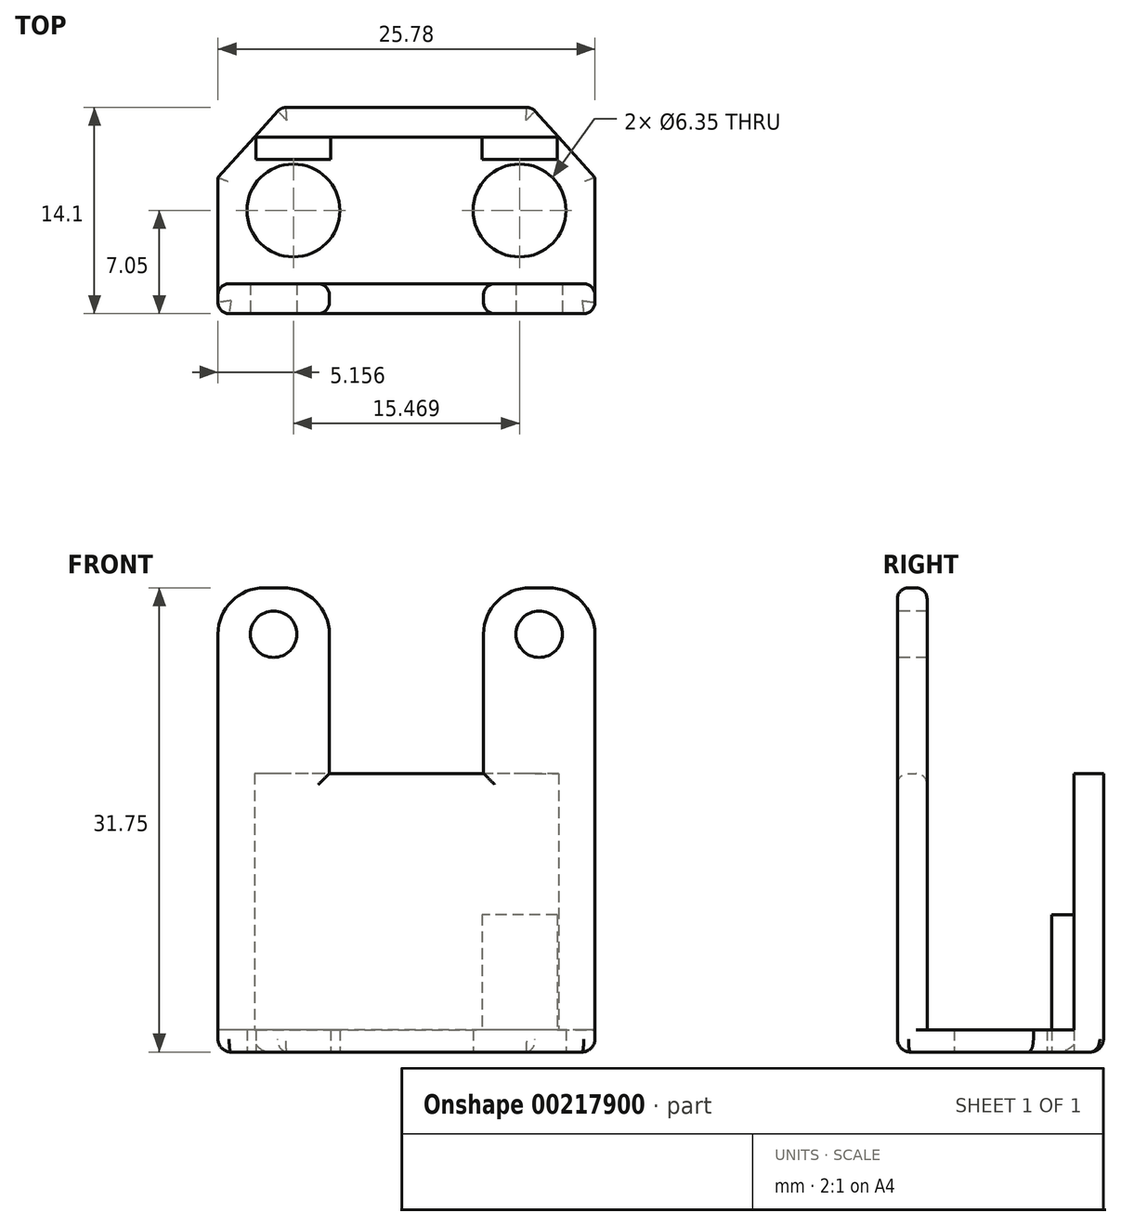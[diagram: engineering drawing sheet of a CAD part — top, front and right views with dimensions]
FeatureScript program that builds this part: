
annotation { "Feature Type Name" : "Feature", "Feature Type Description" : "" }
export const myFeature = defineFeature(function(context is Context, id is Id, definition is map)
    precondition{}
    {
        {
            var Q0;
            Q0=qCreatedBy(makeId("Top.planeOp"),FACE);
            var sketch = newSketch(context, id + "F0", { "sketchPlane" : qUnion([Q0])});
            skLineSegment(sketch, "E0.bottom", {"start": v(10.4, 5.02) * mm, "end": v(-10.4, 5.02) * mm});
            skLineSegment(sketch, "E0.top", {"start": v(12.9, -5.02) * mm, "end": v(-12.9, -5.02) * mm});
            skLineSegment(sketch, "E0.left", {"start": v(12.9, 2.26) * mm, "end": v(12.9, -7.05) * mm});
            skLineSegment(sketch, "E0.right", {"start": v(-12.9, 2.26) * mm, "end": v(-12.9, -7.05) * mm});
            skPoint(sketch, "E0.middle", {"position": v(0, 0) * mm});
            skLineSegment(sketch, "E1.0", {"start": v(14.92, 7.05) * mm, "end": v(-14.92, 7.05) * mm});
            skLineSegment(sketch, "E1.1", {"start": v(14.92, 7.05) * mm, "end": v(14.92, -7.05) * mm});
            skLineSegment(sketch, "E1.2", {"start": v(14.92, -7.05) * mm, "end": v(-14.92, -7.05) * mm});
            skLineSegment(sketch, "E1.3", {"start": v(-14.92, 7.05) * mm, "end": v(-14.92, -7.05) * mm});
            skPoint(sketch, "E2", {"position": v(-7.73, 0) * mm});
            skPoint(sketch, "E2.positionSnap0", {"position": v(-12.9, 0) * mm});
            skLineSegment(sketch, "E3", {"start": v(0, 5.02) * mm, "end": v(0, -5.02) * mm, "construction": true});
            skPoint(sketch, "E4.MirrorP", {"position": v(7.73, 0) * mm});
            skLineSegment(sketch, "E5", {"start": v(-11.78, 3.5) * mm, "end": v(11.78, 3.5) * mm});
            skLineSegment(sketch, "E6", {"start": v(-7.73, 3.5) * mm, "end": v(-7.73, 5.02) * mm, "construction": true});
            skLineSegment(sketch, "E7", {"start": v(-7.73, 3.5) * mm, "end": v(-10.3, 3.5) * mm});
            skLineSegment(sketch, "E8", {"start": v(-10.3, 3.5) * mm, "end": v(-10.3, 5.02) * mm});
            skLineSegment(sketch, "E9.MirrorCS", {"start": v(-5.17, 3.5) * mm, "end": v(-5.17, 5.02) * mm});
            skLineSegment(sketch, "E10.MirrorCS", {"start": v(5.17, 3.5) * mm, "end": v(5.17, 5.02) * mm});
            skLineSegment(sketch, "E11.MirrorCS", {"start": v(10.3, 3.5) * mm, "end": v(10.3, 5.02) * mm});
            skLineSegment(sketch, "E12.MirrorCS", {"start": v(7.73, 3.5) * mm, "end": v(10.3, 3.5) * mm});
            skLineSegment(sketch, "E13.MirrorCS", {"start": v(7.73, 3.5) * mm, "end": v(7.73, 5.02) * mm, "construction": true});
            skPoint(sketch, "E14.endSnap0", {"position": v(-9.02, 3.5) * mm});
            skLineSegment(sketch, "E15", {"start": v(-14.92, 7.05) * mm, "end": v(-8.57, 7.05) * mm});
            skLineSegment(sketch, "E16", {"start": v(-8.57, 7.05) * mm, "end": v(-14.92, 0) * mm});
            skPoint(sketch, "E17.orphan", {"position": v(-12.9, 5.02) * mm});
            skLineSegment(sketch, "E18.MirrorCS", {"start": v(8.57, 7.05) * mm, "end": v(14.92, 0) * mm});
            skPoint(sketch, "E19.orphan", {"position": v(12.9, 5.02) * mm});
            skLineSegment(sketch, "E20", {"start": v(-12.9, -5.02) * mm, "end": v(-14.92, -5.02) * mm});
            skLineSegment(sketch, "E21", {"start": v(12.9, -5.02) * mm, "end": v(14.92, -5.02) * mm});
            skLineSegment(sketch, "E22", {"start": v(-5.27, -5.02) * mm, "end": v(-5.27, -7.05) * mm});
            skLineSegment(sketch, "E23.MirrorCS", {"start": v(5.27, -5.02) * mm, "end": v(5.27, -7.05) * mm});
            skSolve(sketch);
        }
        {
            var Q0;
            Q0=makeQuery(id+"F0.imprint","IMPRINT",FACE,{"disambiguationData":[TD([[makeQuery(id+"F0.imprint","IMPRINT",EDGE,{"derivedFrom":sQuery(id+"F0.wireOp",EDGE,"E0.bottom")}),-1.0]])]});
            var Q1;
            {var subQ0=sQuery(id+"F0.wireOp",EDGE,"E0.top");Q1=makeQuery(id+"F0.imprint","IMPRINT",FACE,{"disambiguationData":[TD([[makeQuery(id+"F0.imprint","IMPRINT",EDGE,{"derivedFrom":subQ0}),-1.0]])]});}
            var Q2;
            {var subQ0=sQuery(id+"F0.wireOp",EDGE,"E0.bottom");Q2=makeQuery(id+"F0.imprint","IMPRINT",FACE,{"disambiguationData":[TD([[makeQuery(id+"F0.imprint","IMPRINT",EDGE,{"derivedFrom":subQ0}),1.0]])]});}
            var Q3;
            {var subQ1=sQuery(id+"F0.wireOp",EDGE,"E7");Q3=makeQuery(id+"F0.imprint","IMPRINT",FACE,{"disambiguationData":[TD([[makeQuery(id+"F0.imprint","IMPRINT",EDGE,{"derivedFrom":subQ1}),-1.0]])]});}
            var Q4;
            {var subQ0=sQuery(id+"F0.wireOp",EDGE,"E10.MirrorCS");Q4=makeQuery(id+"F0.imprint","IMPRINT",FACE,{"disambiguationData":[TD([[makeQuery(id+"F0.imprint","IMPRINT",EDGE,{"derivedFrom":subQ0}),-1.0]])]});}
            extrude(context, id + "F1", {"entities" : qUnion([Q0, Q1, Q2, Q3, Q4]), "depth" : 1.52 * mm});
        }
        {
            var Q0;
            Q0=makeQuery(id+"F0.imprint","IMPRINT",FACE,{"disambiguationData":[TD([[makeQuery(id+"F0.imprint","IMPRINT",EDGE,{"derivedFrom":sQuery(id+"F0.wireOp",EDGE,"E0.bottom")}),-1.0]])]});
            var Q1;
            Q1=makeQuery(id+"F0.imprint","IMPRINT",FACE,{"disambiguationData":[TD([[makeQuery(id+"F0.imprint","IMPRINT",EDGE,{"derivedFrom":sQuery(id+"F0.wireOp",EDGE,"E0.top")}),1.0]])]});
            extrude(context, id + "F2", {"entities" : qUnion([Q0, Q1]), "operationType" : NewBodyOperationType.ADD, "depth" : 19.05 * mm});
        }
        {
            var Q0;
            {var subQ0=sQuery(id+"F0.wireOp",EDGE,"E7");Q0=makeQuery(id+"F0.imprint","IMPRINT",FACE,{"disambiguationData":[TD([[makeQuery(id+"F0.imprint","IMPRINT",EDGE,{"derivedFrom":subQ0}),-1.0]])]});}
            var Q1;
            {var subQ1=sQuery(id+"F0.wireOp",EDGE,"E10.MirrorCS");Q1=makeQuery(id+"F0.imprint","IMPRINT",FACE,{"disambiguationData":[TD([[makeQuery(id+"F0.imprint","IMPRINT",EDGE,{"derivedFrom":subQ1}),-1.0]])]});}
            extrude(context, id + "F3", {"entities" : qUnion([Q0, Q1]), "operationType" : NewBodyOperationType.ADD, "depth" : 9.4 * mm});
        }
        {
            var Q0;
            Q0=sQuery(id+"F0.wireOp",VERTEX,"E2");
            var Q1;
            Q1=sQuery(id+"F0.wireOp",VERTEX,"E4.MirrorP");
            var Q2;
            Q2=makeQuery(id+"F1.opExtrude","SWEPT_BODY",BODY,{"disambiguationData":[OSD([sQuery(id+"F0.wireOp",EDGE,"E1.0"),sQuery(id+"F0.wireOp",EDGE,"E1.1"),sQuery(id+"F0.wireOp",EDGE,"E1.2"),sQuery(id+"F0.wireOp",EDGE,"E1.3")])]});
            hole(context, id + "F4", {"style" : HoleStyle.SIMPLE, "endStyle" : HoleEndStyle.BLIND, "oppositeDirection" : true, "holeDiameter" : 6.35 * mm, "holeDepth" : 6.73 * mm, "locations" : qUnion([Q0, Q1]), "scope" : qUnion([Q2])});
        }
        {
            var Q0;
            {var subQ3=sQuery(id+"F0.wireOp",EDGE,"E22");Q0=makeQuery(id+"F0.imprint","IMPRINT",FACE,{"disambiguationData":[TD([[makeQuery(id+"F0.imprint","IMPRINT",EDGE,{"derivedFrom":subQ3}),-1.0]])]});}
            var Q1;
            {var subQ3=sQuery(id+"F0.wireOp",EDGE,"E23.MirrorCS");Q1=makeQuery(id+"F0.imprint","IMPRINT",FACE,{"disambiguationData":[TD([[makeQuery(id+"F0.imprint","IMPRINT",EDGE,{"derivedFrom":subQ3}),1.0]])]});}
            extrude(context, id + "F5", {"entities" : qUnion([Q0, Q1]), "operationType" : NewBodyOperationType.ADD, "depth" : 31.75 * mm});
        }
        {
            var Q0;
            {var subQ0=sQuery(id+"F0.wireOp",EDGE,"E1.2");Q0=makeQuery(id+"F5.boolean.opBoolean","MERGE",FACE,{"derivedFrom":[makeQuery(id+"F2.opExtrude","SWEPT_FACE",FACE,{"disambiguationData":[OSD([subQ0])]}),makeQuery(id+"F5.opExtrude","SWEPT_FACE",FACE,{"disambiguationData":[OSD([subQ0]),TDD([makeQuery(id+"F0.imprint","IMPRINT",EDGE,{"disambiguationData":[TD([[makeQuery(id+"F0.imprint","INTERSECT",VERTEX,{"derivedFrom":[sQuery(id+"F0.wireOp",EDGE,"E0.left"),subQ0]}),-1.0]])],"derivedFrom":subQ0})])]}),makeQuery(id+"F5.opExtrude","SWEPT_FACE",FACE,{"disambiguationData":[OSD([subQ0]),TDD([makeQuery(id+"F0.imprint","IMPRINT",EDGE,{"disambiguationData":[TD([[makeQuery(id+"F0.imprint","INTERSECT",VERTEX,{"derivedFrom":[sQuery(id+"F0.wireOp",EDGE,"E0.right"),subQ0]}),1.0]])],"derivedFrom":subQ0})])]})]});}
            var sketch = newSketch(context, id + "F6", { "sketchPlane" : qUnion([Q0])});
            skCircle(sketch, "E24", {"center": v(-9.08, 28.57) * mm, "radius": 1.59 * mm});
            skLineSegment(sketch, "E25", {"start": v(0, 19.05) * mm, "end": v(0, 0) * mm, "construction": true});
            skCircle(sketch, "E26.MirrorC", {"center": v(9.08, 28.57) * mm, "radius": 1.59 * mm});
            skSolve(sketch);
        }
        {
            var Q0;
            Q0=sQuery(id+"F6.wireOp",VERTEX,"E24.center");
            var Q1;
            Q1=sQuery(id+"F6.wireOp",VERTEX,"E26.MirrorC.center");
            var Q2;
            Q2=makeQuery(id+"F1.opExtrude","SWEPT_BODY",BODY,{"disambiguationData":[OSD([sQuery(id+"F0.wireOp",EDGE,"E0.top"),sQuery(id+"F0.wireOp",EDGE,"E0.left"),sQuery(id+"F0.wireOp",EDGE,"E0.right"),sQuery(id+"F0.wireOp",EDGE,"E1.0"),sQuery(id+"F0.wireOp",EDGE,"E16"),sQuery(id+"F0.wireOp",EDGE,"E18.MirrorCS")])]});
            hole(context, id + "F7", {"style" : HoleStyle.SIMPLE, "endStyle" : HoleEndStyle.BLIND, "holeDiameter" : 3.17 * mm, "holeDepth" : 9.65 * mm, "locations" : qUnion([Q0, Q1]), "scope" : qUnion([Q2])});
        }
        {
            var Q0;
            Q0=makeQuery(id+"F5.opExtrude","CAP_EDGE",EDGE,{"disambiguationData":[OSD([sQuery(id+"F0.wireOp",EDGE,"E0.right")])],"isStart":false});
            var Q1;
            Q1=makeQuery(id+"F5.opExtrude","CAP_EDGE",EDGE,{"disambiguationData":[OSD([sQuery(id+"F0.wireOp",EDGE,"E22")])],"isStart":false});
            var Q2;
            Q2=makeQuery(id+"F5.opExtrude","CAP_EDGE",EDGE,{"disambiguationData":[OSD([sQuery(id+"F0.wireOp",EDGE,"E23.MirrorCS")])],"isStart":false});
            var Q3;
            Q3=makeQuery(id+"F5.opExtrude","CAP_EDGE",EDGE,{"disambiguationData":[OSD([sQuery(id+"F0.wireOp",EDGE,"E0.left")])],"isStart":false});
            fillet(context, id + "F8", {"entities" : qUnion([Q0, Q1, Q2, Q3]), "radius" : 3.17 * mm, "tangentPropagation" : true, "allowEdgeOverflow" : false});
        }
        {
            var Q0;
            Q0=makeQuery(id+"F2.opExtrude","SWEPT_EDGE",EDGE,{"disambiguationData":[OSD([sQuery(id+"F0.wireOp",EDGE,"E1.2"),sQuery(id+"F0.wireOp",EDGE,"E1.3")])]});
            var Q1;
            Q1=makeQuery(id+"F2.opExtrude","SWEPT_EDGE",EDGE,{"disambiguationData":[OSD([sQuery(id+"F0.wireOp",EDGE,"E1.3"),sQuery(id+"F0.wireOp",EDGE,"E20")])]});
            var Q2;
            Q2=makeQuery(id+"F2.opExtrude","SWEPT_EDGE",EDGE,{"disambiguationData":[OSD([sQuery(id+"F0.wireOp",EDGE,"E1.1"),sQuery(id+"F0.wireOp",EDGE,"E1.2")])]});
            var Q3;
            Q3=makeQuery(id+"F2.opExtrude","SWEPT_EDGE",EDGE,{"disambiguationData":[OSD([sQuery(id+"F0.wireOp",EDGE,"E1.1"),sQuery(id+"F0.wireOp",EDGE,"E21")])]});
            var Q4;
            {var subQ0=sQuery(id+"F0.wireOp",EDGE,"E18.MirrorCS");var subQ1=sQuery(id+"F0.wireOp",EDGE,"E1.0");Q4=makeQuery(id+"F2.boolean.opBoolean","MERGE",EDGE,{"derivedFrom":[makeQuery(id+"F1.opExtrude","SWEPT_EDGE",EDGE,{"disambiguationData":[OSD([subQ1,subQ0])]}),makeQuery(id+"F2.opExtrude","SWEPT_EDGE",EDGE,{"disambiguationData":[OSD([subQ1,subQ0])]})]});}
            var Q5;
            Q5=makeQuery(id+"F2.opExtrude","SWEPT_EDGE",EDGE,{"disambiguationData":[OSD([sQuery(id+"F0.wireOp",EDGE,"E1.1"),sQuery(id+"F0.wireOp",EDGE,"E1.2")])]});
            var Q6;
            Q6=makeQuery(id+"F2.opExtrude","SWEPT_EDGE",EDGE,{"disambiguationData":[OSD([sQuery(id+"F0.wireOp",EDGE,"E1.2"),sQuery(id+"F0.wireOp",EDGE,"E1.3")])]});
            var Q7;
            {var subQ0=sQuery(id+"F0.wireOp",EDGE,"E16");var subQ1=sQuery(id+"F0.wireOp",EDGE,"E15");var subQ2=sQuery(id+"F0.wireOp",EDGE,"E1.0");Q7=makeQuery(id+"F2.boolean.opBoolean","MERGE",EDGE,{"derivedFrom":[makeQuery(id+"F1.opExtrude","SWEPT_EDGE",EDGE,{"disambiguationData":[OSD([subQ2,subQ1,subQ0])]}),makeQuery(id+"F2.opExtrude","SWEPT_EDGE",EDGE,{"disambiguationData":[OSD([subQ2,subQ1,subQ0])]})]});}
            var Q8;
            {var subQ0=sQuery(id+"F0.wireOp",EDGE,"E18.MirrorCS");var subQ1=sQuery(id+"F0.wireOp",EDGE,"E1.0");Q8=makeQuery(id+"F2.boolean.opBoolean","MERGE",EDGE,{"derivedFrom":[makeQuery(id+"F1.opExtrude","SWEPT_EDGE",EDGE,{"disambiguationData":[OSD([subQ1,subQ0])]}),makeQuery(id+"F2.opExtrude","SWEPT_EDGE",EDGE,{"disambiguationData":[OSD([subQ1,subQ0])]})]});}
            var Q9;
            {var subQ0=sQuery(id+"F0.wireOp",EDGE,"E1.2");var subQ1=sQuery(id+"F0.wireOp",EDGE,"E0.right");Q9=makeQuery(id+"F8.opFillet","BLEND_EDGE",EDGE,{"blendedFrom":[makeQuery(id+"F5.opExtrude","CAP_EDGE",EDGE,{"disambiguationData":[OSD([subQ1])],"isStart":false}),makeQuery(id+"F5.boolean.opBoolean","MERGE",FACE,{"derivedFrom":[makeQuery(id+"F2.opExtrude","SWEPT_FACE",FACE,{"disambiguationData":[OSD([subQ0])]}),makeQuery(id+"F5.opExtrude","SWEPT_FACE",FACE,{"disambiguationData":[OSD([subQ0]),TDD([makeQuery(id+"F0.imprint","IMPRINT",EDGE,{"disambiguationData":[TD([[makeQuery(id+"F0.imprint","INTERSECT",VERTEX,{"derivedFrom":[sQuery(id+"F0.wireOp",EDGE,"E0.left"),subQ0]}),-1.0]])],"derivedFrom":subQ0})])]}),makeQuery(id+"F5.opExtrude","SWEPT_FACE",FACE,{"disambiguationData":[OSD([subQ0]),TDD([makeQuery(id+"F0.imprint","IMPRINT",EDGE,{"disambiguationData":[TD([[makeQuery(id+"F0.imprint","INTERSECT",VERTEX,{"derivedFrom":[subQ1,subQ0]}),1.0]])],"derivedFrom":subQ0})])]})]})],"blendedInto":[makeQuery(id+"F5.boolean.opBoolean","MERGE",FACE,{"derivedFrom":[makeQuery(id+"F2.opExtrude","SWEPT_FACE",FACE,{"disambiguationData":[OSD([subQ0])]}),makeQuery(id+"F5.opExtrude","SWEPT_FACE",FACE,{"disambiguationData":[OSD([subQ0]),TDD([makeQuery(id+"F0.imprint","IMPRINT",EDGE,{"disambiguationData":[TD([[makeQuery(id+"F0.imprint","INTERSECT",VERTEX,{"derivedFrom":[sQuery(id+"F0.wireOp",EDGE,"E0.left"),subQ0]}),-1.0]])],"derivedFrom":subQ0})])]}),makeQuery(id+"F5.opExtrude","SWEPT_FACE",FACE,{"disambiguationData":[OSD([subQ0]),TDD([makeQuery(id+"F0.imprint","IMPRINT",EDGE,{"disambiguationData":[TD([[makeQuery(id+"F0.imprint","INTERSECT",VERTEX,{"derivedFrom":[subQ1,subQ0]}),1.0]])],"derivedFrom":subQ0})])]})]})]});}
            var Q10;
            {var subQ0=sQuery(id+"F0.wireOp",EDGE,"E0.right");var subQ1=sQuery(id+"F0.wireOp",EDGE,"E0.top");Q10=makeQuery(id+"F8.opFillet","BLEND_EDGE",EDGE,{"blendedFrom":[makeQuery(id+"F5.opExtrude","CAP_EDGE",EDGE,{"disambiguationData":[OSD([subQ0])],"isStart":false}),makeQuery(id+"F5.boolean.opBoolean","MERGE",FACE,{"derivedFrom":[makeQuery(id+"F2.opExtrude","SWEPT_FACE",FACE,{"disambiguationData":[OSD([subQ1])]}),makeQuery(id+"F5.opExtrude","SWEPT_FACE",FACE,{"disambiguationData":[OSD([subQ1]),TDD([makeQuery(id+"F0.imprint","IMPRINT",EDGE,{"disambiguationData":[TD([[makeQuery(id+"F0.imprint","INTERSECT",VERTEX,{"derivedFrom":[subQ1,sQuery(id+"F0.wireOp",EDGE,"E23.MirrorCS")]}),1.0]])],"derivedFrom":subQ1})])]}),makeQuery(id+"F5.opExtrude","SWEPT_FACE",FACE,{"disambiguationData":[OSD([subQ1]),TDD([makeQuery(id+"F0.imprint","IMPRINT",EDGE,{"disambiguationData":[TD([[makeQuery(id+"F0.imprint","INTERSECT",VERTEX,{"derivedFrom":[subQ1,sQuery(id+"F0.wireOp",EDGE,"E22")]}),-1.0]])],"derivedFrom":subQ1})])]})]})],"blendedInto":[makeQuery(id+"F5.boolean.opBoolean","MERGE",FACE,{"derivedFrom":[makeQuery(id+"F2.opExtrude","SWEPT_FACE",FACE,{"disambiguationData":[OSD([subQ1])]}),makeQuery(id+"F5.opExtrude","SWEPT_FACE",FACE,{"disambiguationData":[OSD([subQ1]),TDD([makeQuery(id+"F0.imprint","IMPRINT",EDGE,{"disambiguationData":[TD([[makeQuery(id+"F0.imprint","INTERSECT",VERTEX,{"derivedFrom":[subQ1,sQuery(id+"F0.wireOp",EDGE,"E23.MirrorCS")]}),1.0]])],"derivedFrom":subQ1})])]}),makeQuery(id+"F5.opExtrude","SWEPT_FACE",FACE,{"disambiguationData":[OSD([subQ1]),TDD([makeQuery(id+"F0.imprint","IMPRINT",EDGE,{"disambiguationData":[TD([[makeQuery(id+"F0.imprint","INTERSECT",VERTEX,{"derivedFrom":[subQ1,sQuery(id+"F0.wireOp",EDGE,"E22")]}),-1.0]])],"derivedFrom":subQ1})])]})]})]});}
            var Q11;
            {var subQ0=sQuery(id+"F0.wireOp",EDGE,"E1.2");Q11=makeQuery(id+"F5.opExtrude","CAP_EDGE",EDGE,{"disambiguationData":[OSD([subQ0]),TDD([makeQuery(id+"F0.imprint","IMPRINT",EDGE,{"disambiguationData":[TD([[makeQuery(id+"F0.imprint","INTERSECT",VERTEX,{"derivedFrom":[sQuery(id+"F0.wireOp",EDGE,"E0.right"),subQ0]}),1.0]])],"derivedFrom":subQ0})])],"isStart":false});}
            var Q12;
            {var subQ0=sQuery(id+"F0.wireOp",EDGE,"E0.top");Q12=makeQuery(id+"F5.opExtrude","CAP_EDGE",EDGE,{"disambiguationData":[OSD([subQ0]),TDD([makeQuery(id+"F0.imprint","IMPRINT",EDGE,{"disambiguationData":[TD([[makeQuery(id+"F0.imprint","INTERSECT",VERTEX,{"derivedFrom":[subQ0,sQuery(id+"F0.wireOp",EDGE,"E22")]}),-1.0]])],"derivedFrom":subQ0})])],"isStart":false});}
            var Q13;
            {var subQ0=sQuery(id+"F0.wireOp",EDGE,"E0.top");var subQ1=sQuery(id+"F0.wireOp",EDGE,"E22");Q13=makeQuery(id+"F8.opFillet","BLEND_EDGE",EDGE,{"blendedFrom":[makeQuery(id+"F5.opExtrude","CAP_EDGE",EDGE,{"disambiguationData":[OSD([subQ1])],"isStart":false}),makeQuery(id+"F5.boolean.opBoolean","MERGE",FACE,{"derivedFrom":[makeQuery(id+"F2.opExtrude","SWEPT_FACE",FACE,{"disambiguationData":[OSD([subQ0])]}),makeQuery(id+"F5.opExtrude","SWEPT_FACE",FACE,{"disambiguationData":[OSD([subQ0]),TDD([makeQuery(id+"F0.imprint","IMPRINT",EDGE,{"disambiguationData":[TD([[makeQuery(id+"F0.imprint","INTERSECT",VERTEX,{"derivedFrom":[subQ0,sQuery(id+"F0.wireOp",EDGE,"E23.MirrorCS")]}),1.0]])],"derivedFrom":subQ0})])]}),makeQuery(id+"F5.opExtrude","SWEPT_FACE",FACE,{"disambiguationData":[OSD([subQ0]),TDD([makeQuery(id+"F0.imprint","IMPRINT",EDGE,{"disambiguationData":[TD([[makeQuery(id+"F0.imprint","INTERSECT",VERTEX,{"derivedFrom":[subQ0,subQ1]}),-1.0]])],"derivedFrom":subQ0})])]})]})],"blendedInto":[makeQuery(id+"F5.boolean.opBoolean","MERGE",FACE,{"derivedFrom":[makeQuery(id+"F2.opExtrude","SWEPT_FACE",FACE,{"disambiguationData":[OSD([subQ0])]}),makeQuery(id+"F5.opExtrude","SWEPT_FACE",FACE,{"disambiguationData":[OSD([subQ0]),TDD([makeQuery(id+"F0.imprint","IMPRINT",EDGE,{"disambiguationData":[TD([[makeQuery(id+"F0.imprint","INTERSECT",VERTEX,{"derivedFrom":[subQ0,sQuery(id+"F0.wireOp",EDGE,"E23.MirrorCS")]}),1.0]])],"derivedFrom":subQ0})])]}),makeQuery(id+"F5.opExtrude","SWEPT_FACE",FACE,{"disambiguationData":[OSD([subQ0]),TDD([makeQuery(id+"F0.imprint","IMPRINT",EDGE,{"disambiguationData":[TD([[makeQuery(id+"F0.imprint","INTERSECT",VERTEX,{"derivedFrom":[subQ0,subQ1]}),-1.0]])],"derivedFrom":subQ0})])]})]})]});}
            var Q14;
            {var subQ0=sQuery(id+"F0.wireOp",EDGE,"E1.2");var subQ1=sQuery(id+"F0.wireOp",EDGE,"E22");Q14=makeQuery(id+"F8.opFillet","BLEND_EDGE",EDGE,{"blendedFrom":[makeQuery(id+"F5.opExtrude","CAP_EDGE",EDGE,{"disambiguationData":[OSD([subQ1])],"isStart":false}),makeQuery(id+"F5.boolean.opBoolean","MERGE",FACE,{"derivedFrom":[makeQuery(id+"F2.opExtrude","SWEPT_FACE",FACE,{"disambiguationData":[OSD([subQ0])]}),makeQuery(id+"F5.opExtrude","SWEPT_FACE",FACE,{"disambiguationData":[OSD([subQ0]),TDD([makeQuery(id+"F0.imprint","IMPRINT",EDGE,{"disambiguationData":[TD([[makeQuery(id+"F0.imprint","INTERSECT",VERTEX,{"derivedFrom":[sQuery(id+"F0.wireOp",EDGE,"E0.left"),subQ0]}),-1.0]])],"derivedFrom":subQ0})])]}),makeQuery(id+"F5.opExtrude","SWEPT_FACE",FACE,{"disambiguationData":[OSD([subQ0]),TDD([makeQuery(id+"F0.imprint","IMPRINT",EDGE,{"disambiguationData":[TD([[makeQuery(id+"F0.imprint","INTERSECT",VERTEX,{"derivedFrom":[sQuery(id+"F0.wireOp",EDGE,"E0.right"),subQ0]}),1.0]])],"derivedFrom":subQ0})])]})]})],"blendedInto":[makeQuery(id+"F5.boolean.opBoolean","MERGE",FACE,{"derivedFrom":[makeQuery(id+"F2.opExtrude","SWEPT_FACE",FACE,{"disambiguationData":[OSD([subQ0])]}),makeQuery(id+"F5.opExtrude","SWEPT_FACE",FACE,{"disambiguationData":[OSD([subQ0]),TDD([makeQuery(id+"F0.imprint","IMPRINT",EDGE,{"disambiguationData":[TD([[makeQuery(id+"F0.imprint","INTERSECT",VERTEX,{"derivedFrom":[sQuery(id+"F0.wireOp",EDGE,"E0.left"),subQ0]}),-1.0]])],"derivedFrom":subQ0})])]}),makeQuery(id+"F5.opExtrude","SWEPT_FACE",FACE,{"disambiguationData":[OSD([subQ0]),TDD([makeQuery(id+"F0.imprint","IMPRINT",EDGE,{"disambiguationData":[TD([[makeQuery(id+"F0.imprint","INTERSECT",VERTEX,{"derivedFrom":[sQuery(id+"F0.wireOp",EDGE,"E0.right"),subQ0]}),1.0]])],"derivedFrom":subQ0})])]})]})]});}
            var Q15;
            Q15=makeQuery(id+"F5.opExtrude","SWEPT_EDGE",EDGE,{"disambiguationData":[OSD([sQuery(id+"F0.wireOp",EDGE,"E1.2"),sQuery(id+"F0.wireOp",EDGE,"E22")])]});
            var Q16;
            Q16=makeQuery(id+"F2.opExtrude","CAP_EDGE",EDGE,{"disambiguationData":[OSD([sQuery(id+"F0.wireOp",EDGE,"E1.2")])],"isStart":false});
            var Q17;
            Q17=makeQuery(id+"F5.opExtrude","SWEPT_EDGE",EDGE,{"disambiguationData":[OSD([sQuery(id+"F0.wireOp",EDGE,"E1.2"),sQuery(id+"F0.wireOp",EDGE,"E23.MirrorCS")])]});
            var Q18;
            {var subQ0=sQuery(id+"F0.wireOp",EDGE,"E1.2");var subQ1=sQuery(id+"F0.wireOp",EDGE,"E23.MirrorCS");Q18=makeQuery(id+"F8.opFillet","BLEND_EDGE",EDGE,{"blendedFrom":[makeQuery(id+"F5.opExtrude","CAP_EDGE",EDGE,{"disambiguationData":[OSD([subQ1])],"isStart":false}),makeQuery(id+"F5.boolean.opBoolean","MERGE",FACE,{"derivedFrom":[makeQuery(id+"F2.opExtrude","SWEPT_FACE",FACE,{"disambiguationData":[OSD([subQ0])]}),makeQuery(id+"F5.opExtrude","SWEPT_FACE",FACE,{"disambiguationData":[OSD([subQ0]),TDD([makeQuery(id+"F0.imprint","IMPRINT",EDGE,{"disambiguationData":[TD([[makeQuery(id+"F0.imprint","INTERSECT",VERTEX,{"derivedFrom":[sQuery(id+"F0.wireOp",EDGE,"E0.left"),subQ0]}),-1.0]])],"derivedFrom":subQ0})])]}),makeQuery(id+"F5.opExtrude","SWEPT_FACE",FACE,{"disambiguationData":[OSD([subQ0]),TDD([makeQuery(id+"F0.imprint","IMPRINT",EDGE,{"disambiguationData":[TD([[makeQuery(id+"F0.imprint","INTERSECT",VERTEX,{"derivedFrom":[sQuery(id+"F0.wireOp",EDGE,"E0.right"),subQ0]}),1.0]])],"derivedFrom":subQ0})])]})]})],"blendedInto":[makeQuery(id+"F5.boolean.opBoolean","MERGE",FACE,{"derivedFrom":[makeQuery(id+"F2.opExtrude","SWEPT_FACE",FACE,{"disambiguationData":[OSD([subQ0])]}),makeQuery(id+"F5.opExtrude","SWEPT_FACE",FACE,{"disambiguationData":[OSD([subQ0]),TDD([makeQuery(id+"F0.imprint","IMPRINT",EDGE,{"disambiguationData":[TD([[makeQuery(id+"F0.imprint","INTERSECT",VERTEX,{"derivedFrom":[sQuery(id+"F0.wireOp",EDGE,"E0.left"),subQ0]}),-1.0]])],"derivedFrom":subQ0})])]}),makeQuery(id+"F5.opExtrude","SWEPT_FACE",FACE,{"disambiguationData":[OSD([subQ0]),TDD([makeQuery(id+"F0.imprint","IMPRINT",EDGE,{"disambiguationData":[TD([[makeQuery(id+"F0.imprint","INTERSECT",VERTEX,{"derivedFrom":[sQuery(id+"F0.wireOp",EDGE,"E0.right"),subQ0]}),1.0]])],"derivedFrom":subQ0})])]})]})]});}
            var Q19;
            {var subQ0=sQuery(id+"F0.wireOp",EDGE,"E1.2");Q19=makeQuery(id+"F5.opExtrude","CAP_EDGE",EDGE,{"disambiguationData":[OSD([subQ0]),TDD([makeQuery(id+"F0.imprint","IMPRINT",EDGE,{"disambiguationData":[TD([[makeQuery(id+"F0.imprint","INTERSECT",VERTEX,{"derivedFrom":[sQuery(id+"F0.wireOp",EDGE,"E0.left"),subQ0]}),-1.0]])],"derivedFrom":subQ0})])],"isStart":false});}
            var Q20;
            {var subQ0=sQuery(id+"F0.wireOp",EDGE,"E1.2");var subQ1=sQuery(id+"F0.wireOp",EDGE,"E0.left");Q20=makeQuery(id+"F8.opFillet","BLEND_EDGE",EDGE,{"blendedFrom":[makeQuery(id+"F5.opExtrude","CAP_EDGE",EDGE,{"disambiguationData":[OSD([subQ1])],"isStart":false}),makeQuery(id+"F5.boolean.opBoolean","MERGE",FACE,{"derivedFrom":[makeQuery(id+"F2.opExtrude","SWEPT_FACE",FACE,{"disambiguationData":[OSD([subQ0])]}),makeQuery(id+"F5.opExtrude","SWEPT_FACE",FACE,{"disambiguationData":[OSD([subQ0]),TDD([makeQuery(id+"F0.imprint","IMPRINT",EDGE,{"disambiguationData":[TD([[makeQuery(id+"F0.imprint","INTERSECT",VERTEX,{"derivedFrom":[subQ1,subQ0]}),-1.0]])],"derivedFrom":subQ0})])]}),makeQuery(id+"F5.opExtrude","SWEPT_FACE",FACE,{"disambiguationData":[OSD([subQ0]),TDD([makeQuery(id+"F0.imprint","IMPRINT",EDGE,{"disambiguationData":[TD([[makeQuery(id+"F0.imprint","INTERSECT",VERTEX,{"derivedFrom":[sQuery(id+"F0.wireOp",EDGE,"E0.right"),subQ0]}),1.0]])],"derivedFrom":subQ0})])]})]})],"blendedInto":[makeQuery(id+"F5.boolean.opBoolean","MERGE",FACE,{"derivedFrom":[makeQuery(id+"F2.opExtrude","SWEPT_FACE",FACE,{"disambiguationData":[OSD([subQ0])]}),makeQuery(id+"F5.opExtrude","SWEPT_FACE",FACE,{"disambiguationData":[OSD([subQ0]),TDD([makeQuery(id+"F0.imprint","IMPRINT",EDGE,{"disambiguationData":[TD([[makeQuery(id+"F0.imprint","INTERSECT",VERTEX,{"derivedFrom":[subQ1,subQ0]}),-1.0]])],"derivedFrom":subQ0})])]}),makeQuery(id+"F5.opExtrude","SWEPT_FACE",FACE,{"disambiguationData":[OSD([subQ0]),TDD([makeQuery(id+"F0.imprint","IMPRINT",EDGE,{"disambiguationData":[TD([[makeQuery(id+"F0.imprint","INTERSECT",VERTEX,{"derivedFrom":[sQuery(id+"F0.wireOp",EDGE,"E0.right"),subQ0]}),1.0]])],"derivedFrom":subQ0})])]})]})]});}
            var Q21;
            Q21=makeQuery(id+"F5.opExtrude","SWEPT_EDGE",EDGE,{"disambiguationData":[OSD([sQuery(id+"F0.wireOp",EDGE,"E0.top"),sQuery(id+"F0.wireOp",EDGE,"E22")])]});
            var Q22;
            Q22=makeQuery(id+"F2.opExtrude","CAP_EDGE",EDGE,{"disambiguationData":[OSD([sQuery(id+"F0.wireOp",EDGE,"E0.top")])],"isStart":false});
            var Q23;
            Q23=makeQuery(id+"F5.opExtrude","SWEPT_EDGE",EDGE,{"disambiguationData":[OSD([sQuery(id+"F0.wireOp",EDGE,"E0.top"),sQuery(id+"F0.wireOp",EDGE,"E23.MirrorCS")])]});
            var Q24;
            {var subQ0=sQuery(id+"F0.wireOp",EDGE,"E0.top");var subQ1=sQuery(id+"F0.wireOp",EDGE,"E23.MirrorCS");Q24=makeQuery(id+"F8.opFillet","BLEND_EDGE",EDGE,{"blendedFrom":[makeQuery(id+"F5.opExtrude","CAP_EDGE",EDGE,{"disambiguationData":[OSD([subQ1])],"isStart":false}),makeQuery(id+"F5.boolean.opBoolean","MERGE",FACE,{"derivedFrom":[makeQuery(id+"F2.opExtrude","SWEPT_FACE",FACE,{"disambiguationData":[OSD([subQ0])]}),makeQuery(id+"F5.opExtrude","SWEPT_FACE",FACE,{"disambiguationData":[OSD([subQ0]),TDD([makeQuery(id+"F0.imprint","IMPRINT",EDGE,{"disambiguationData":[TD([[makeQuery(id+"F0.imprint","INTERSECT",VERTEX,{"derivedFrom":[subQ0,subQ1]}),1.0]])],"derivedFrom":subQ0})])]}),makeQuery(id+"F5.opExtrude","SWEPT_FACE",FACE,{"disambiguationData":[OSD([subQ0]),TDD([makeQuery(id+"F0.imprint","IMPRINT",EDGE,{"disambiguationData":[TD([[makeQuery(id+"F0.imprint","INTERSECT",VERTEX,{"derivedFrom":[subQ0,sQuery(id+"F0.wireOp",EDGE,"E22")]}),-1.0]])],"derivedFrom":subQ0})])]})]})],"blendedInto":[makeQuery(id+"F5.boolean.opBoolean","MERGE",FACE,{"derivedFrom":[makeQuery(id+"F2.opExtrude","SWEPT_FACE",FACE,{"disambiguationData":[OSD([subQ0])]}),makeQuery(id+"F5.opExtrude","SWEPT_FACE",FACE,{"disambiguationData":[OSD([subQ0]),TDD([makeQuery(id+"F0.imprint","IMPRINT",EDGE,{"disambiguationData":[TD([[makeQuery(id+"F0.imprint","INTERSECT",VERTEX,{"derivedFrom":[subQ0,subQ1]}),1.0]])],"derivedFrom":subQ0})])]}),makeQuery(id+"F5.opExtrude","SWEPT_FACE",FACE,{"disambiguationData":[OSD([subQ0]),TDD([makeQuery(id+"F0.imprint","IMPRINT",EDGE,{"disambiguationData":[TD([[makeQuery(id+"F0.imprint","INTERSECT",VERTEX,{"derivedFrom":[subQ0,sQuery(id+"F0.wireOp",EDGE,"E22")]}),-1.0]])],"derivedFrom":subQ0})])]})]})]});}
            var Q25;
            {var subQ0=sQuery(id+"F0.wireOp",EDGE,"E0.top");Q25=makeQuery(id+"F5.opExtrude","CAP_EDGE",EDGE,{"disambiguationData":[OSD([subQ0]),TDD([makeQuery(id+"F0.imprint","IMPRINT",EDGE,{"disambiguationData":[TD([[makeQuery(id+"F0.imprint","INTERSECT",VERTEX,{"derivedFrom":[subQ0,sQuery(id+"F0.wireOp",EDGE,"E23.MirrorCS")]}),1.0]])],"derivedFrom":subQ0})])],"isStart":false});}
            var Q26;
            {var subQ0=sQuery(id+"F0.wireOp",EDGE,"E0.top");var subQ1=sQuery(id+"F0.wireOp",EDGE,"E0.left");Q26=makeQuery(id+"F8.opFillet","BLEND_EDGE",EDGE,{"blendedFrom":[makeQuery(id+"F5.opExtrude","CAP_EDGE",EDGE,{"disambiguationData":[OSD([subQ1])],"isStart":false}),makeQuery(id+"F5.boolean.opBoolean","MERGE",FACE,{"derivedFrom":[makeQuery(id+"F2.opExtrude","SWEPT_FACE",FACE,{"disambiguationData":[OSD([subQ0])]}),makeQuery(id+"F5.opExtrude","SWEPT_FACE",FACE,{"disambiguationData":[OSD([subQ0]),TDD([makeQuery(id+"F0.imprint","IMPRINT",EDGE,{"disambiguationData":[TD([[makeQuery(id+"F0.imprint","INTERSECT",VERTEX,{"derivedFrom":[subQ0,sQuery(id+"F0.wireOp",EDGE,"E23.MirrorCS")]}),1.0]])],"derivedFrom":subQ0})])]}),makeQuery(id+"F5.opExtrude","SWEPT_FACE",FACE,{"disambiguationData":[OSD([subQ0]),TDD([makeQuery(id+"F0.imprint","IMPRINT",EDGE,{"disambiguationData":[TD([[makeQuery(id+"F0.imprint","INTERSECT",VERTEX,{"derivedFrom":[subQ0,sQuery(id+"F0.wireOp",EDGE,"E22")]}),-1.0]])],"derivedFrom":subQ0})])]})]})],"blendedInto":[makeQuery(id+"F5.boolean.opBoolean","MERGE",FACE,{"derivedFrom":[makeQuery(id+"F2.opExtrude","SWEPT_FACE",FACE,{"disambiguationData":[OSD([subQ0])]}),makeQuery(id+"F5.opExtrude","SWEPT_FACE",FACE,{"disambiguationData":[OSD([subQ0]),TDD([makeQuery(id+"F0.imprint","IMPRINT",EDGE,{"disambiguationData":[TD([[makeQuery(id+"F0.imprint","INTERSECT",VERTEX,{"derivedFrom":[subQ0,sQuery(id+"F0.wireOp",EDGE,"E23.MirrorCS")]}),1.0]])],"derivedFrom":subQ0})])]}),makeQuery(id+"F5.opExtrude","SWEPT_FACE",FACE,{"disambiguationData":[OSD([subQ0]),TDD([makeQuery(id+"F0.imprint","IMPRINT",EDGE,{"disambiguationData":[TD([[makeQuery(id+"F0.imprint","INTERSECT",VERTEX,{"derivedFrom":[subQ0,sQuery(id+"F0.wireOp",EDGE,"E22")]}),-1.0]])],"derivedFrom":subQ0})])]})]})]});}
            fillet(context, id + "F9", {"entities" : qUnion([Q0, Q1, Q2, Q3, Q4, Q5, Q6, Q7, Q8, Q9, Q10, Q11, Q12, Q13, Q14, Q15, Q16, Q17, Q18, Q19, Q20, Q21, Q22, Q23, Q24, Q25, Q26]), "radius" : 0.76 * mm, "tangentPropagation" : true, "allowEdgeOverflow" : false});
        }
        {
            var Q0;
            Q0=makeQuery(id+"F1.opExtrude","CAP_EDGE",EDGE,{"disambiguationData":[OSD([sQuery(id+"F0.wireOp",EDGE,"E1.0")])],"isStart":true});
            var Q1;
            Q1=makeQuery(id+"F2.opExtrude","CAP_EDGE",EDGE,{"disambiguationData":[OSD([sQuery(id+"F0.wireOp",EDGE,"E1.2")])],"isStart":true});
            var Q2;
            Q2=makeQuery(id+"F1.opExtrude","CAP_EDGE",EDGE,{"disambiguationData":[OSD([sQuery(id+"F0.wireOp",EDGE,"E0.right")])],"isStart":true});
            var Q3;
            Q3=makeQuery(id+"F1.opExtrude","CAP_EDGE",EDGE,{"disambiguationData":[OSD([sQuery(id+"F0.wireOp",EDGE,"E16")])],"isStart":true});
            var Q4;
            {var subQ0=sQuery(id+"F0.wireOp",EDGE,"E0.top");var subQ1=sQuery(id+"F0.wireOp",EDGE,"E16");var subQ2=sQuery(id+"F0.wireOp",EDGE,"E1.0");var subQ3=sQuery(id+"F0.wireOp",EDGE,"E15");Q4=makeQuery(id+"F9.opFillet","BLEND_EDGE",EDGE,{"blendedFrom":[makeQuery(id+"F2.boolean.opBoolean","MERGE",EDGE,{"derivedFrom":[makeQuery(id+"F1.opExtrude","SWEPT_EDGE",EDGE,{"disambiguationData":[OSD([subQ2,subQ3,subQ1])]}),makeQuery(id+"F2.opExtrude","SWEPT_EDGE",EDGE,{"disambiguationData":[OSD([subQ2,subQ3,subQ1])]})]}),makeQuery(id+"F2.boolean.opBoolean","MERGE",FACE,{"derivedFrom":[makeQuery(id+"F1.opExtrude","CAP_FACE",FACE,{"disambiguationData":[OSD([subQ0,sQuery(id+"F0.wireOp",EDGE,"E0.left"),sQuery(id+"F0.wireOp",EDGE,"E0.right"),subQ2,subQ1,sQuery(id+"F0.wireOp",EDGE,"E18.MirrorCS")])],"isStart":true}),makeQuery(id+"F2.opExtrude","CAP_FACE",FACE,{"disambiguationData":[OSD([subQ0,sQuery(id+"F0.wireOp",EDGE,"E1.1"),sQuery(id+"F0.wireOp",EDGE,"E1.2"),sQuery(id+"F0.wireOp",EDGE,"E1.3"),sQuery(id+"F0.wireOp",EDGE,"E20"),sQuery(id+"F0.wireOp",EDGE,"E21")])],"isStart":true})]})],"blendedInto":[makeQuery(id+"F2.boolean.opBoolean","MERGE",FACE,{"derivedFrom":[makeQuery(id+"F1.opExtrude","CAP_FACE",FACE,{"disambiguationData":[OSD([subQ0,sQuery(id+"F0.wireOp",EDGE,"E0.left"),sQuery(id+"F0.wireOp",EDGE,"E0.right"),subQ2,subQ1,sQuery(id+"F0.wireOp",EDGE,"E18.MirrorCS")])],"isStart":true}),makeQuery(id+"F2.opExtrude","CAP_FACE",FACE,{"disambiguationData":[OSD([subQ0,sQuery(id+"F0.wireOp",EDGE,"E1.1"),sQuery(id+"F0.wireOp",EDGE,"E1.2"),sQuery(id+"F0.wireOp",EDGE,"E1.3"),sQuery(id+"F0.wireOp",EDGE,"E20"),sQuery(id+"F0.wireOp",EDGE,"E21")])],"isStart":true})]})]});}
            var Q5;
            {var subQ0=sQuery(id+"F0.wireOp",EDGE,"E0.top");var subQ1=sQuery(id+"F0.wireOp",EDGE,"E18.MirrorCS");var subQ2=sQuery(id+"F0.wireOp",EDGE,"E1.0");Q5=makeQuery(id+"F9.opFillet","BLEND_EDGE",EDGE,{"blendedFrom":[makeQuery(id+"F2.boolean.opBoolean","MERGE",EDGE,{"derivedFrom":[makeQuery(id+"F1.opExtrude","SWEPT_EDGE",EDGE,{"disambiguationData":[OSD([subQ2,subQ1])]}),makeQuery(id+"F2.opExtrude","SWEPT_EDGE",EDGE,{"disambiguationData":[OSD([subQ2,subQ1])]})]}),makeQuery(id+"F2.boolean.opBoolean","MERGE",FACE,{"derivedFrom":[makeQuery(id+"F1.opExtrude","CAP_FACE",FACE,{"disambiguationData":[OSD([subQ0,sQuery(id+"F0.wireOp",EDGE,"E0.left"),sQuery(id+"F0.wireOp",EDGE,"E0.right"),subQ2,sQuery(id+"F0.wireOp",EDGE,"E16"),subQ1])],"isStart":true}),makeQuery(id+"F2.opExtrude","CAP_FACE",FACE,{"disambiguationData":[OSD([subQ0,sQuery(id+"F0.wireOp",EDGE,"E1.1"),sQuery(id+"F0.wireOp",EDGE,"E1.2"),sQuery(id+"F0.wireOp",EDGE,"E1.3"),sQuery(id+"F0.wireOp",EDGE,"E20"),sQuery(id+"F0.wireOp",EDGE,"E21")])],"isStart":true})]})],"blendedInto":[makeQuery(id+"F2.boolean.opBoolean","MERGE",FACE,{"derivedFrom":[makeQuery(id+"F1.opExtrude","CAP_FACE",FACE,{"disambiguationData":[OSD([subQ0,sQuery(id+"F0.wireOp",EDGE,"E0.left"),sQuery(id+"F0.wireOp",EDGE,"E0.right"),subQ2,sQuery(id+"F0.wireOp",EDGE,"E16"),subQ1])],"isStart":true}),makeQuery(id+"F2.opExtrude","CAP_FACE",FACE,{"disambiguationData":[OSD([subQ0,sQuery(id+"F0.wireOp",EDGE,"E1.1"),sQuery(id+"F0.wireOp",EDGE,"E1.2"),sQuery(id+"F0.wireOp",EDGE,"E1.3"),sQuery(id+"F0.wireOp",EDGE,"E20"),sQuery(id+"F0.wireOp",EDGE,"E21")])],"isStart":true})]})]});}
            var Q6;
            Q6=makeQuery(id+"F1.opExtrude","CAP_EDGE",EDGE,{"disambiguationData":[OSD([sQuery(id+"F0.wireOp",EDGE,"E18.MirrorCS")])],"isStart":true});
            var Q7;
            Q7=makeQuery(id+"F1.opExtrude","CAP_EDGE",EDGE,{"disambiguationData":[OSD([sQuery(id+"F0.wireOp",EDGE,"E0.left")])],"isStart":true});
            var Q8;
            {var subQ0=sQuery(id+"F0.wireOp",EDGE,"E1.2");var subQ1=sQuery(id+"F0.wireOp",EDGE,"E1.1");var subQ2=sQuery(id+"F0.wireOp",EDGE,"E0.top");Q8=makeQuery(id+"F9.opFillet","BLEND_EDGE",EDGE,{"blendedFrom":[makeQuery(id+"F2.opExtrude","SWEPT_EDGE",EDGE,{"disambiguationData":[OSD([subQ1,subQ0])]}),makeQuery(id+"F2.boolean.opBoolean","MERGE",FACE,{"derivedFrom":[makeQuery(id+"F1.opExtrude","CAP_FACE",FACE,{"disambiguationData":[OSD([subQ2,sQuery(id+"F0.wireOp",EDGE,"E0.left"),sQuery(id+"F0.wireOp",EDGE,"E0.right"),sQuery(id+"F0.wireOp",EDGE,"E1.0"),sQuery(id+"F0.wireOp",EDGE,"E16"),sQuery(id+"F0.wireOp",EDGE,"E18.MirrorCS")])],"isStart":true}),makeQuery(id+"F2.opExtrude","CAP_FACE",FACE,{"disambiguationData":[OSD([subQ2,subQ1,subQ0,sQuery(id+"F0.wireOp",EDGE,"E1.3"),sQuery(id+"F0.wireOp",EDGE,"E20"),sQuery(id+"F0.wireOp",EDGE,"E21")])],"isStart":true})]})],"blendedInto":[makeQuery(id+"F2.boolean.opBoolean","MERGE",FACE,{"derivedFrom":[makeQuery(id+"F1.opExtrude","CAP_FACE",FACE,{"disambiguationData":[OSD([subQ2,sQuery(id+"F0.wireOp",EDGE,"E0.left"),sQuery(id+"F0.wireOp",EDGE,"E0.right"),sQuery(id+"F0.wireOp",EDGE,"E1.0"),sQuery(id+"F0.wireOp",EDGE,"E16"),sQuery(id+"F0.wireOp",EDGE,"E18.MirrorCS")])],"isStart":true}),makeQuery(id+"F2.opExtrude","CAP_FACE",FACE,{"disambiguationData":[OSD([subQ2,subQ1,subQ0,sQuery(id+"F0.wireOp",EDGE,"E1.3"),sQuery(id+"F0.wireOp",EDGE,"E20"),sQuery(id+"F0.wireOp",EDGE,"E21")])],"isStart":true})]})]});}
            var Q9;
            {var subQ0=sQuery(id+"F0.wireOp",EDGE,"E21");var subQ1=sQuery(id+"F0.wireOp",EDGE,"E1.1");var subQ2=sQuery(id+"F0.wireOp",EDGE,"E0.top");Q9=makeQuery(id+"F9.opFillet","BLEND_EDGE",EDGE,{"blendedFrom":[makeQuery(id+"F2.opExtrude","SWEPT_EDGE",EDGE,{"disambiguationData":[OSD([subQ1,subQ0])]}),makeQuery(id+"F2.boolean.opBoolean","MERGE",FACE,{"derivedFrom":[makeQuery(id+"F1.opExtrude","CAP_FACE",FACE,{"disambiguationData":[OSD([subQ2,sQuery(id+"F0.wireOp",EDGE,"E0.left"),sQuery(id+"F0.wireOp",EDGE,"E0.right"),sQuery(id+"F0.wireOp",EDGE,"E1.0"),sQuery(id+"F0.wireOp",EDGE,"E16"),sQuery(id+"F0.wireOp",EDGE,"E18.MirrorCS")])],"isStart":true}),makeQuery(id+"F2.opExtrude","CAP_FACE",FACE,{"disambiguationData":[OSD([subQ2,subQ1,sQuery(id+"F0.wireOp",EDGE,"E1.2"),sQuery(id+"F0.wireOp",EDGE,"E1.3"),sQuery(id+"F0.wireOp",EDGE,"E20"),subQ0])],"isStart":true})]})],"blendedInto":[makeQuery(id+"F2.boolean.opBoolean","MERGE",FACE,{"derivedFrom":[makeQuery(id+"F1.opExtrude","CAP_FACE",FACE,{"disambiguationData":[OSD([subQ2,sQuery(id+"F0.wireOp",EDGE,"E0.left"),sQuery(id+"F0.wireOp",EDGE,"E0.right"),sQuery(id+"F0.wireOp",EDGE,"E1.0"),sQuery(id+"F0.wireOp",EDGE,"E16"),sQuery(id+"F0.wireOp",EDGE,"E18.MirrorCS")])],"isStart":true}),makeQuery(id+"F2.opExtrude","CAP_FACE",FACE,{"disambiguationData":[OSD([subQ2,subQ1,sQuery(id+"F0.wireOp",EDGE,"E1.2"),sQuery(id+"F0.wireOp",EDGE,"E1.3"),sQuery(id+"F0.wireOp",EDGE,"E20"),subQ0])],"isStart":true})]})]});}
            var Q10;
            {var subQ0=sQuery(id+"F0.wireOp",EDGE,"E21");var subQ1=sQuery(id+"F0.wireOp",EDGE,"E20");var subQ3=sQuery(id+"F0.wireOp",EDGE,"E0.top");var subQ4=sQuery(id+"F0.wireOp",EDGE,"E0.left");Q10=makeQuery(id+"F2.boolean.opBoolean","SPLIT",EDGE,{"disambiguationData":[TD([makeQuery(id+"F1.opExtrude","SWEPT_FACE",FACE,{"disambiguationData":[OSD([subQ4])]})])],"derivedFrom":makeQuery(id+"F2.opExtrude","CAP_EDGE",EDGE,{"disambiguationData":[OSD([subQ3,subQ1,subQ0])],"isStart":true})});}
            var Q11;
            {var subQ0=sQuery(id+"F0.wireOp",EDGE,"E1.3");var subQ1=sQuery(id+"F0.wireOp",EDGE,"E1.2");var subQ2=sQuery(id+"F0.wireOp",EDGE,"E0.top");Q11=makeQuery(id+"F9.opFillet","BLEND_EDGE",EDGE,{"blendedFrom":[makeQuery(id+"F2.opExtrude","SWEPT_EDGE",EDGE,{"disambiguationData":[OSD([subQ1,subQ0])]}),makeQuery(id+"F2.boolean.opBoolean","MERGE",FACE,{"derivedFrom":[makeQuery(id+"F1.opExtrude","CAP_FACE",FACE,{"disambiguationData":[OSD([subQ2,sQuery(id+"F0.wireOp",EDGE,"E0.left"),sQuery(id+"F0.wireOp",EDGE,"E0.right"),sQuery(id+"F0.wireOp",EDGE,"E1.0"),sQuery(id+"F0.wireOp",EDGE,"E16"),sQuery(id+"F0.wireOp",EDGE,"E18.MirrorCS")])],"isStart":true}),makeQuery(id+"F2.opExtrude","CAP_FACE",FACE,{"disambiguationData":[OSD([subQ2,sQuery(id+"F0.wireOp",EDGE,"E1.1"),subQ1,subQ0,sQuery(id+"F0.wireOp",EDGE,"E20"),sQuery(id+"F0.wireOp",EDGE,"E21")])],"isStart":true})]})],"blendedInto":[makeQuery(id+"F2.boolean.opBoolean","MERGE",FACE,{"derivedFrom":[makeQuery(id+"F1.opExtrude","CAP_FACE",FACE,{"disambiguationData":[OSD([subQ2,sQuery(id+"F0.wireOp",EDGE,"E0.left"),sQuery(id+"F0.wireOp",EDGE,"E0.right"),sQuery(id+"F0.wireOp",EDGE,"E1.0"),sQuery(id+"F0.wireOp",EDGE,"E16"),sQuery(id+"F0.wireOp",EDGE,"E18.MirrorCS")])],"isStart":true}),makeQuery(id+"F2.opExtrude","CAP_FACE",FACE,{"disambiguationData":[OSD([subQ2,sQuery(id+"F0.wireOp",EDGE,"E1.1"),subQ1,subQ0,sQuery(id+"F0.wireOp",EDGE,"E20"),sQuery(id+"F0.wireOp",EDGE,"E21")])],"isStart":true})]})]});}
            var Q12;
            {var subQ0=sQuery(id+"F0.wireOp",EDGE,"E20");var subQ1=sQuery(id+"F0.wireOp",EDGE,"E1.3");var subQ2=sQuery(id+"F0.wireOp",EDGE,"E0.top");Q12=makeQuery(id+"F9.opFillet","BLEND_EDGE",EDGE,{"blendedFrom":[makeQuery(id+"F2.opExtrude","SWEPT_EDGE",EDGE,{"disambiguationData":[OSD([subQ1,subQ0])]}),makeQuery(id+"F2.boolean.opBoolean","MERGE",FACE,{"derivedFrom":[makeQuery(id+"F1.opExtrude","CAP_FACE",FACE,{"disambiguationData":[OSD([subQ2,sQuery(id+"F0.wireOp",EDGE,"E0.left"),sQuery(id+"F0.wireOp",EDGE,"E0.right"),sQuery(id+"F0.wireOp",EDGE,"E1.0"),sQuery(id+"F0.wireOp",EDGE,"E16"),sQuery(id+"F0.wireOp",EDGE,"E18.MirrorCS")])],"isStart":true}),makeQuery(id+"F2.opExtrude","CAP_FACE",FACE,{"disambiguationData":[OSD([subQ2,sQuery(id+"F0.wireOp",EDGE,"E1.1"),sQuery(id+"F0.wireOp",EDGE,"E1.2"),subQ1,subQ0,sQuery(id+"F0.wireOp",EDGE,"E21")])],"isStart":true})]})],"blendedInto":[makeQuery(id+"F2.boolean.opBoolean","MERGE",FACE,{"derivedFrom":[makeQuery(id+"F1.opExtrude","CAP_FACE",FACE,{"disambiguationData":[OSD([subQ2,sQuery(id+"F0.wireOp",EDGE,"E0.left"),sQuery(id+"F0.wireOp",EDGE,"E0.right"),sQuery(id+"F0.wireOp",EDGE,"E1.0"),sQuery(id+"F0.wireOp",EDGE,"E16"),sQuery(id+"F0.wireOp",EDGE,"E18.MirrorCS")])],"isStart":true}),makeQuery(id+"F2.opExtrude","CAP_FACE",FACE,{"disambiguationData":[OSD([subQ2,sQuery(id+"F0.wireOp",EDGE,"E1.1"),sQuery(id+"F0.wireOp",EDGE,"E1.2"),subQ1,subQ0,sQuery(id+"F0.wireOp",EDGE,"E21")])],"isStart":true})]})]});}
            fillet(context, id + "F10", {"entities" : qUnion([Q0, Q1, Q2, Q3, Q4, Q5, Q6, Q7, Q8, Q9, Q10, Q11, Q12]), "radius" : 0.89 * mm, "tangentPropagation" : true, "allowEdgeOverflow" : false});
        }
    });
